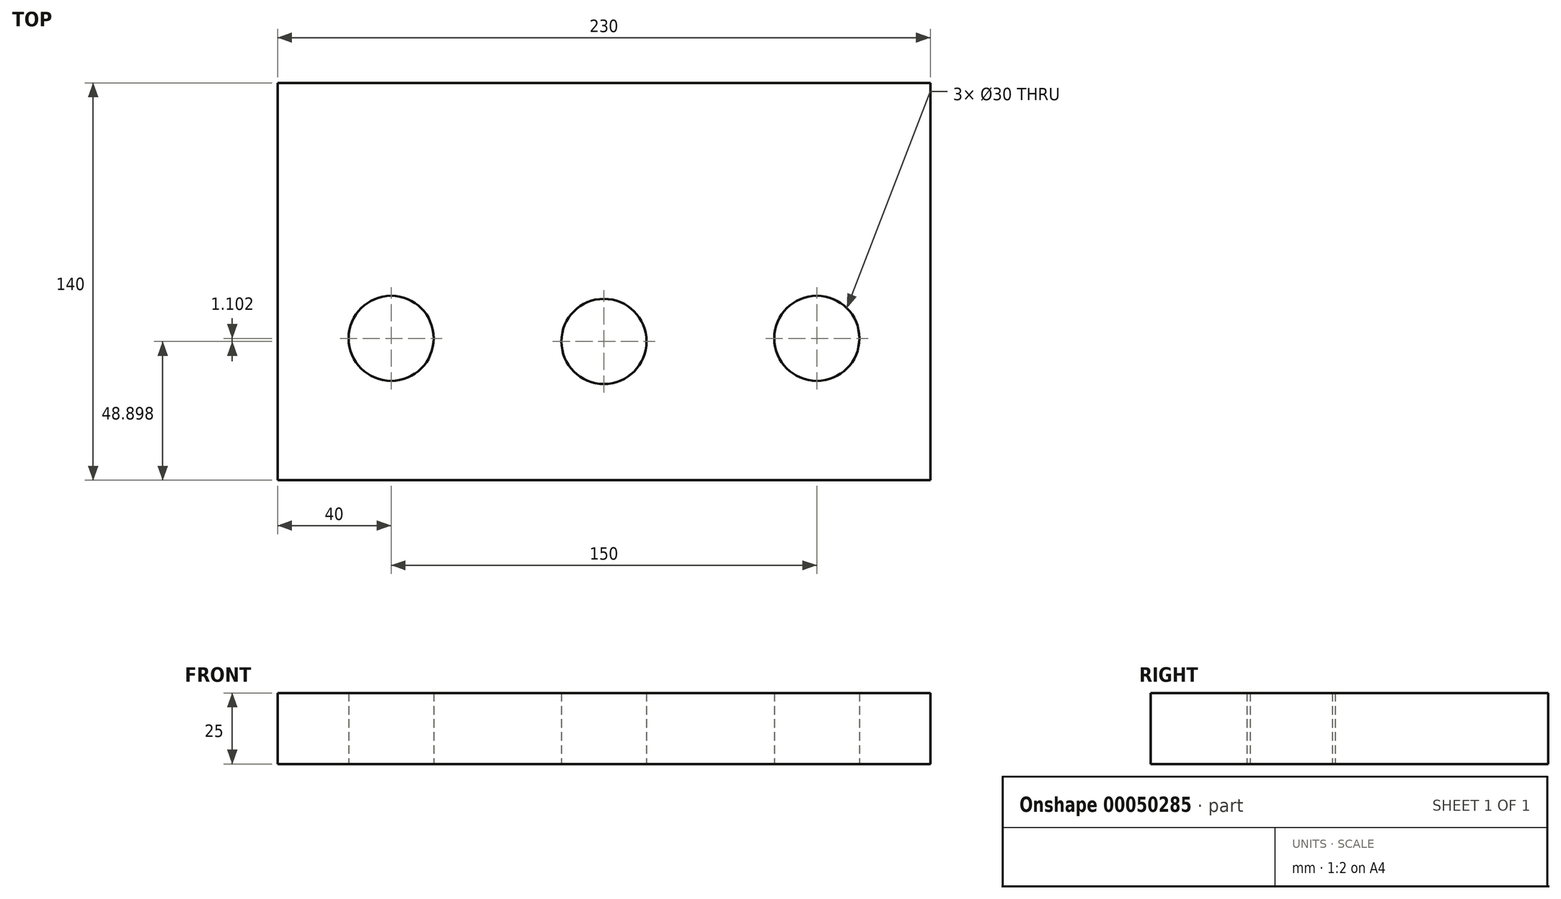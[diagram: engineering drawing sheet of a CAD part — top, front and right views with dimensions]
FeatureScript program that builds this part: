
annotation { "Feature Type Name" : "Feature", "Feature Type Description" : "" }
export const myFeature = defineFeature(function(context is Context, id is Id, definition is map)
    precondition{}
    {
        {
            var Q0;
            Q0=qCreatedBy(makeId("Top.planeOp"),FACE);
            var sketch = newSketch(context, id + "F0", { "sketchPlane" : qUnion([Q0])});
            skLineSegment(sketch, "E0.rect.bottom", {"start": v(115, 70) * mm, "end": v(-115, 70) * mm});
            skLineSegment(sketch, "E0.rect.top", {"start": v(115, -70) * mm, "end": v(-115, -70) * mm});
            skLineSegment(sketch, "E0.rect.left", {"start": v(115, 70) * mm, "end": v(115, -70) * mm});
            skLineSegment(sketch, "E0.rect.right", {"start": v(-115, 70) * mm, "end": v(-115, -70) * mm});
            skPoint(sketch, "E0.rect.middle", {"position": v(0, 0) * mm});
            skCircle(sketch, "E1", {"center": v(0, -21.1) * mm, "radius": 15 * mm});
            skCircle(sketch, "E2", {"center": v(-75, -20) * mm, "radius": 15 * mm});
            skCircle(sketch, "E3", {"center": v(75, -20) * mm, "radius": 15 * mm});
            skSolve(sketch);
        }
        {
            var Q0;
            Q0=makeQuery(id+"F0.imprint","IMPRINT",FACE,{"disambiguationData":[TD([[makeQuery(id+"F0.imprint","IMPRINT",EDGE,{"derivedFrom":sQuery(id+"F0.wireOp",EDGE,"E0.rect.bottom")}),1.0]])]});
            extrude(context, id + "F1", {"entities" : qUnion([Q0]), "depth" : 25 * mm});
        }
    });
